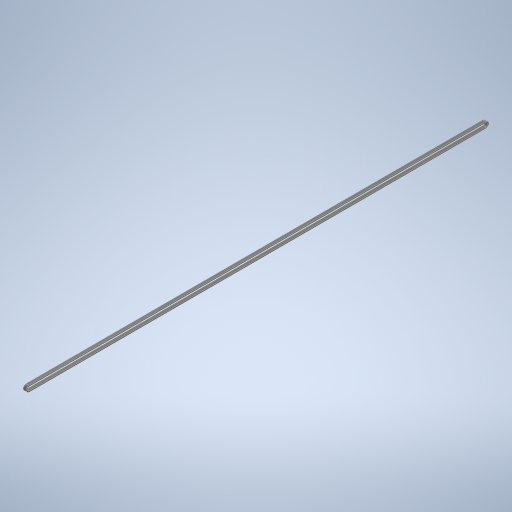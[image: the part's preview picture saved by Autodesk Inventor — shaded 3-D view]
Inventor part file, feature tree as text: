
AUTODESK INVENTOR PART (.ipt)
format: ipt  version: 2023 (Build 270158000, 158)  size: 261,120 bytes
history: native  units: in
note: dims shown in document units (in); Inventor stores cm internally (conversion verified against a paired STEP export)
features: sketch x2, plane x1, sweep x1
ambient origin geometry x8: Origin, YZ Plane, XZ Plane, XY Plane, X Axis, Y Axis, Z Axis, Center Point
bodies: Solid1 (feature_tree)
feature tree (4):
  sketch  "Sketch1"  dims[d0=35.301in d1=0.1505in]
  plane  "Work Plane1"
  sweep  "Sweep1"
  sketch  "Sketch2"  dims[d2=0.1505in d3=0.1505in d4=-0.1505in d5=0.0787in d6=0.0in d7=0.2362in d8=0.0in d9=0.0in]
